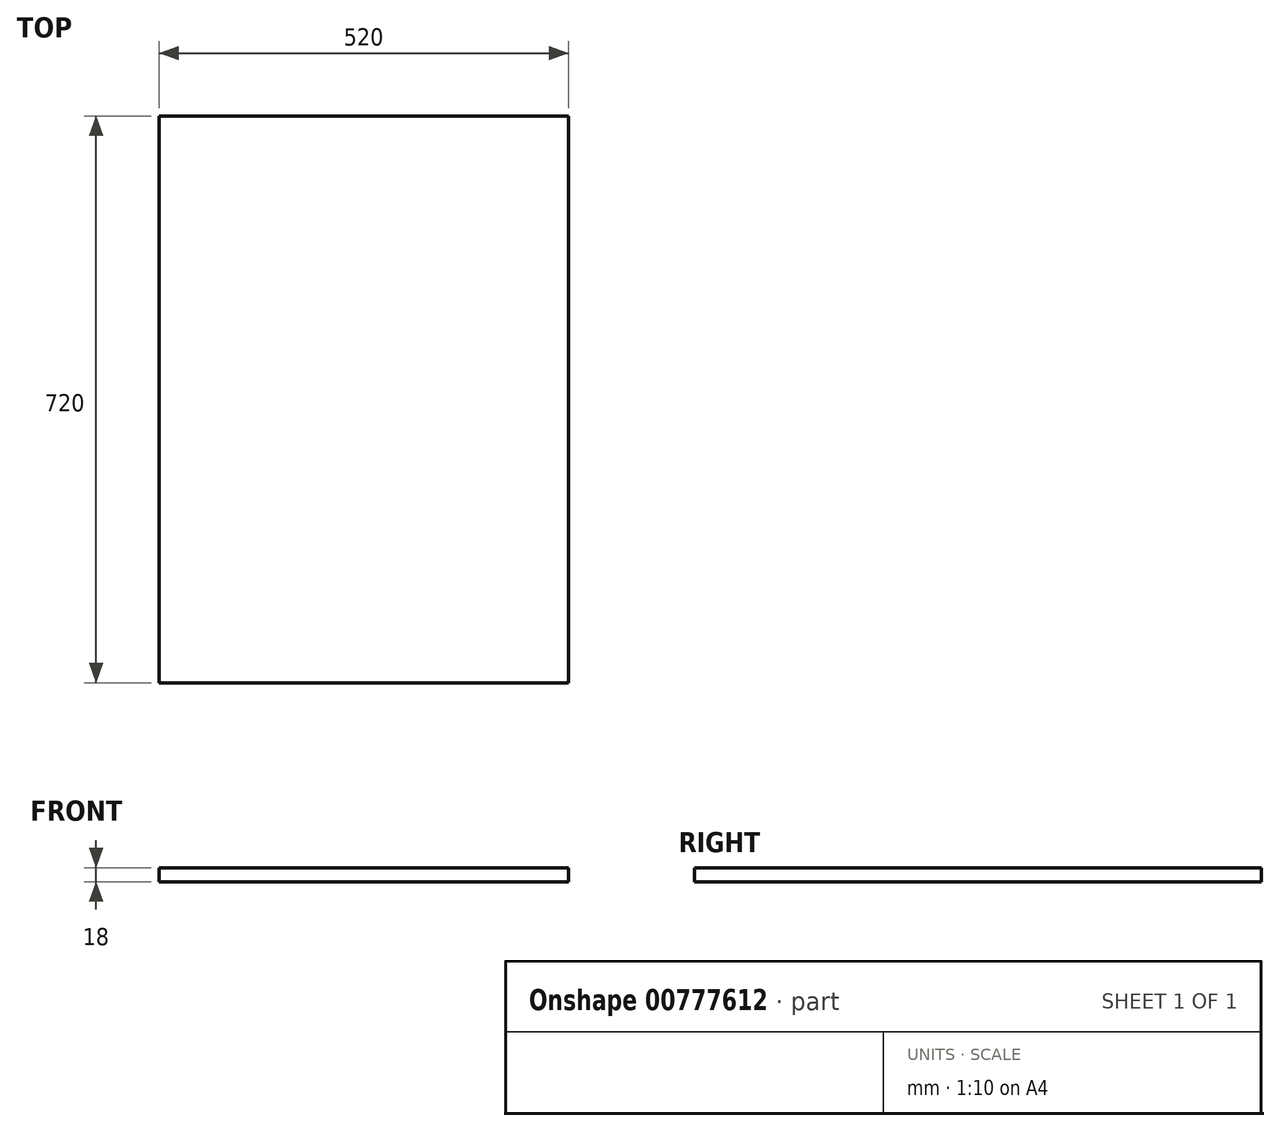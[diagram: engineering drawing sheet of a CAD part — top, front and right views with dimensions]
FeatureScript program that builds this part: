
annotation { "Feature Type Name" : "Feature", "Feature Type Description" : "" }
export const myFeature = defineFeature(function(context is Context, id is Id, definition is map)
    precondition{}
    {
        {
            var Q0;
            Q0=qCreatedBy(makeId("Top.planeOp"),FACE);
            var sketch = newSketch(context, id + "F0", { "sketchPlane" : qUnion([Q0])});
            skLineSegment(sketch, "E0.bottom", {"start": v(-260, 360) * mm, "end": v(260, 360) * mm});
            skLineSegment(sketch, "E0.top", {"start": v(-260, -360) * mm, "end": v(260, -360) * mm});
            skLineSegment(sketch, "E0.left", {"start": v(-260, 360) * mm, "end": v(-260, -360) * mm});
            skLineSegment(sketch, "E0.right", {"start": v(260, 360) * mm, "end": v(260, -360) * mm});
            skPoint(sketch, "E0.middle", {"position": v(0, 0) * mm});
            skSolve(sketch);
        }
        {
            var Q0;
            Q0=makeQuery(id+"F0.imprint","IMPRINT",FACE,{"disambiguationData":[TD([[makeQuery(id+"F0.imprint","IMPRINT",EDGE,{"derivedFrom":sQuery(id+"F0.wireOp",EDGE,"E0.bottom")}),-1.0]])]});
            extrude(context, id + "F1", {"entities" : qUnion([Q0]), "depth" : 18 * mm, "offsetDistance" : 25 * mm});
        }
    });
